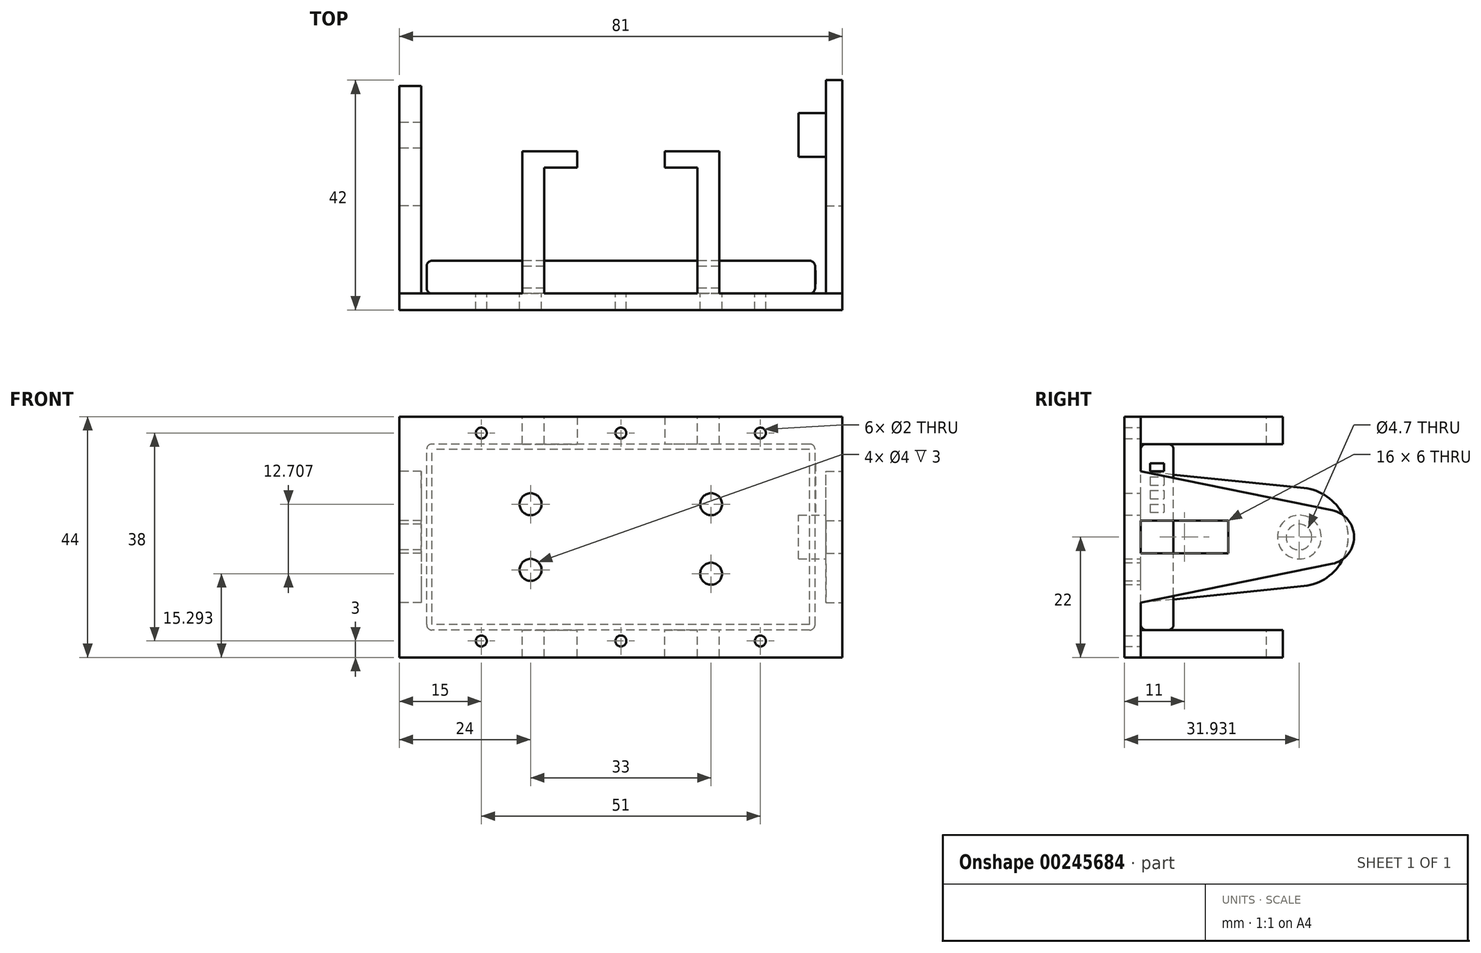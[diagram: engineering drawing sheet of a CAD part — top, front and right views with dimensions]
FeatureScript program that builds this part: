
annotation { "Feature Type Name" : "Feature", "Feature Type Description" : "" }
export const myFeature = defineFeature(function(context is Context, id is Id, definition is map)
    precondition{}
    {
        {
            var Q0;
            Q0=qCreatedBy(makeId("Front.planeOp"),FACE);
            var sketch = newSketch(context, id + "F0", { "sketchPlane" : qUnion([Q0])});
            skLineSegment(sketch, "E0.bottom", {"start": v(35.5, -17) * mm, "end": v(-35.5, -17) * mm});
            skLineSegment(sketch, "E0.top", {"start": v(35.5, 17) * mm, "end": v(-35.5, 17) * mm});
            skLineSegment(sketch, "E0.left", {"start": v(35.5, -17) * mm, "end": v(35.5, 17) * mm});
            skLineSegment(sketch, "E0.right", {"start": v(-35.5, -17) * mm, "end": v(-35.5, 17) * mm});
            skPoint(sketch, "E0.middle", {"position": v(0, 0) * mm});
            skSolve(sketch);
        }
        {
            var Q0;
            Q0=qSketchRegion(id+"F0",true);
            extrude(context, id + "F1", {"entities" : qUnion([Q0]), "endBound" : BoundingType.SYMMETRIC, "depth" : 6 * mm});
        }
        {
            var Q0;
            Q0=makeQuery(id+"F1.opExtrude","CAP_EDGE",EDGE,{"disambiguationData":[OSD([sQuery(id+"F0.wireOp",EDGE,"E0.top")])],"isStart":false});
            var Q1;
            Q1=makeQuery(id+"F1.opExtrude","CAP_EDGE",EDGE,{"disambiguationData":[OSD([sQuery(id+"F0.wireOp",EDGE,"E0.top")])],"isStart":true});
            var Q2;
            Q2=makeQuery(id+"F1.opExtrude","CAP_EDGE",EDGE,{"disambiguationData":[OSD([sQuery(id+"F0.wireOp",EDGE,"E0.left")])],"isStart":false});
            var Q3;
            Q3=makeQuery(id+"F1.opExtrude","CAP_EDGE",EDGE,{"disambiguationData":[OSD([sQuery(id+"F0.wireOp",EDGE,"E0.left")])],"isStart":true});
            var Q4;
            Q4=makeQuery(id+"F1.opExtrude","CAP_EDGE",EDGE,{"disambiguationData":[OSD([sQuery(id+"F0.wireOp",EDGE,"E0.bottom")])],"isStart":false});
            var Q5;
            Q5=makeQuery(id+"F1.opExtrude","SWEPT_EDGE",EDGE,{"disambiguationData":[OSD([sQuery(id+"F0.wireOp",EDGE,"E0.bottom"),sQuery(id+"F0.wireOp",EDGE,"E0.left")])]});
            var Q6;
            Q6=makeQuery(id+"F1.opExtrude","SWEPT_EDGE",EDGE,{"disambiguationData":[OSD([sQuery(id+"F0.wireOp",EDGE,"E0.top"),sQuery(id+"F0.wireOp",EDGE,"E0.right")])]});
            var Q7;
            Q7=makeQuery(id+"F1.opExtrude","CAP_EDGE",EDGE,{"disambiguationData":[OSD([sQuery(id+"F0.wireOp",EDGE,"E0.right")])],"isStart":false});
            var Q8;
            Q8=makeQuery(id+"F1.opExtrude","CAP_EDGE",EDGE,{"disambiguationData":[OSD([sQuery(id+"F0.wireOp",EDGE,"E0.right")])],"isStart":true});
            var Q9;
            Q9=makeQuery(id+"F1.opExtrude","CAP_EDGE",EDGE,{"disambiguationData":[OSD([sQuery(id+"F0.wireOp",EDGE,"E0.bottom")])],"isStart":true});
            var Q10;
            Q10=makeQuery(id+"F1.opExtrude","SWEPT_EDGE",EDGE,{"disambiguationData":[OSD([sQuery(id+"F0.wireOp",EDGE,"E0.bottom"),sQuery(id+"F0.wireOp",EDGE,"E0.right")])]});
            var Q11;
            Q11=makeQuery(id+"F1.opExtrude","SWEPT_EDGE",EDGE,{"disambiguationData":[OSD([sQuery(id+"F0.wireOp",EDGE,"E0.top"),sQuery(id+"F0.wireOp",EDGE,"E0.left")])]});
            fillet(context, id + "F2", {"entities" : qUnion([Q0, Q1, Q2, Q3, Q4, Q5, Q6, Q7, Q8, Q9, Q10, Q11]), "radius" : 1 * mm, "tangentPropagation" : true, "allowEdgeOverflow" : false});
        }
        {
            var Q0;
            Q0=makeQuery(id+"F1.opExtrude","SWEPT_FACE",FACE,{"disambiguationData":[OSD([sQuery(id+"F0.wireOp",EDGE,"E0.left")])]});
            var sketch = newSketch(context, id + "F3", { "sketchPlane" : qUnion([Q0])});
            skLineSegment(sketch, "E1.bottom", {"start": v(-1.25, 13.5) * mm, "end": v(1.25, 13.5) * mm});
            skLineSegment(sketch, "E1.top", {"start": v(-1.25, 12) * mm, "end": v(1.25, 12) * mm});
            skLineSegment(sketch, "E1.left", {"start": v(-1.25, 13.5) * mm, "end": v(-1.25, 12) * mm});
            skLineSegment(sketch, "E1.right", {"start": v(1.25, 13.5) * mm, "end": v(1.25, 12) * mm});
            skLineSegment(sketch, "E2.bottom", {"start": v(-1.25, 11) * mm, "end": v(1.25, 11) * mm});
            skLineSegment(sketch, "E2.top", {"start": v(-1.25, 9.5) * mm, "end": v(1.25, 9.5) * mm});
            skLineSegment(sketch, "E2.left", {"start": v(-1.25, 11) * mm, "end": v(-1.25, 9.5) * mm});
            skLineSegment(sketch, "E2.right", {"start": v(1.25, 11) * mm, "end": v(1.25, 9.5) * mm});
            skLineSegment(sketch, "E3.bottom", {"start": v(-1.25, 8.5) * mm, "end": v(1.25, 8.5) * mm});
            skLineSegment(sketch, "E3.top", {"start": v(-1.25, 7) * mm, "end": v(1.25, 7) * mm});
            skLineSegment(sketch, "E3.left", {"start": v(-1.25, 8.5) * mm, "end": v(-1.25, 7) * mm});
            skLineSegment(sketch, "E3.right", {"start": v(1.25, 8.5) * mm, "end": v(1.25, 7) * mm});
            skLineSegment(sketch, "E4.bottom", {"start": v(-1.25, 6) * mm, "end": v(1.25, 6) * mm});
            skLineSegment(sketch, "E4.top", {"start": v(-1.25, 4.5) * mm, "end": v(1.25, 4.5) * mm});
            skLineSegment(sketch, "E4.left", {"start": v(-1.25, 6) * mm, "end": v(-1.25, 4.5) * mm});
            skLineSegment(sketch, "E4.right", {"start": v(1.25, 6) * mm, "end": v(1.25, 4.5) * mm});
            skSolve(sketch);
        }
        {
            var Q0;
            Q0=qSketchRegion(id+"F3",true);
            extrude(context, id + "F4", {"entities" : qUnion([Q0]), "operationType" : NewBodyOperationType.ADD, "depth" : 0.1 * mm});
        }
        {
            var Q0;
            Q0=makeQuery(id+"F1.opExtrude","CAP_FACE",FACE,{"disambiguationData":[OSD([sQuery(id+"F0.wireOp",EDGE,"E0.bottom"),sQuery(id+"F0.wireOp",EDGE,"E0.top"),sQuery(id+"F0.wireOp",EDGE,"E0.left"),sQuery(id+"F0.wireOp",EDGE,"E0.right")])],"isStart":false});
            var sketch = newSketch(context, id + "F5", { "sketchPlane" : qUnion([Q0])});
            skLineSegment(sketch, "E5.0", {"start": v(40.5, 22) * mm, "end": v(-40.5, 22) * mm});
            skLineSegment(sketch, "E5.1", {"start": v(40.5, -22) * mm, "end": v(40.5, 22) * mm});
            skLineSegment(sketch, "E5.2", {"start": v(-40.5, -22) * mm, "end": v(40.5, -22) * mm});
            skLineSegment(sketch, "E5.3", {"start": v(-40.5, 22) * mm, "end": v(-40.5, -22) * mm});
            skCircle(sketch, "E6", {"center": v(16.5, 6) * mm, "radius": 2 * mm});
            skCircle(sketch, "E7", {"center": v(16.5, -6.7) * mm, "radius": 2 * mm});
            skCircle(sketch, "E8", {"center": v(-16.5, 6) * mm, "radius": 2 * mm});
            skCircle(sketch, "E9", {"center": v(-16.5, -6) * mm, "radius": 2 * mm});
            skSolve(sketch);
        }
        {
            var Q0;
            Q0=qSketchRegion(id+"F5",true);
            extrude(context, id + "F6", {"entities" : qUnion([Q0]), "depth" : 3 * mm});
        }
        {
            var Q0;
            Q0=makeQuery(id+"F6.opExtrude","SWEPT_FACE",FACE,{"disambiguationData":[OSD([sQuery(id+"F5.wireOp",EDGE,"E5.3")])]});
            var sketch = newSketch(context, id + "F7", { "sketchPlane" : qUnion([Q0])});
            skCircle(sketch, "E10", {"center": v(-25.93, 0) * mm, "radius": 9 * mm});
            skLineSegment(sketch, "E11", {"start": v(-26.84, -8.95) * mm, "end": v(3, -12) * mm});
            skLineSegment(sketch, "E12", {"start": v(-26.84, 8.95) * mm, "end": v(3, 12) * mm});
            skLineSegment(sketch, "E13", {"start": v(3, 12) * mm, "end": v(3, 3) * mm});
            skLineSegment(sketch, "E14.bottom", {"start": v(-13, -3) * mm, "end": v(3, -3) * mm});
            skLineSegment(sketch, "E14.top", {"start": v(-13, 3) * mm, "end": v(3, 3) * mm});
            skLineSegment(sketch, "E14.left", {"start": v(-13, -3) * mm, "end": v(-13, 3) * mm});
            skLineSegment(sketch, "E15.trimOffspring", {"start": v(3, -3) * mm, "end": v(3, -12) * mm});
            skCircle(sketch, "E16", {"center": v(-25.93, 0) * mm, "radius": 2.35 * mm});
            skSolve(sketch);
        }
        {
            var Q0;
            Q0=qSketchRegion(id+"F7",true);
            extrude(context, id + "F8", {"entities" : qUnion([Q0]), "operationType" : NewBodyOperationType.ADD, "oppositeDirection" : true, "depth" : 4 * mm});
        }
        {
            var Q0;
            Q0=makeQuery(id+"F6.opExtrude","SWEPT_FACE",FACE,{"disambiguationData":[OSD([sQuery(id+"F5.wireOp",EDGE,"E5.1")])]});
            var sketch = newSketch(context, id + "F9", { "sketchPlane" : qUnion([Q0])});
            skCircle(sketch, "E17", {"center": v(31, 0) * mm, "radius": 5 * mm});
            skLineSegment(sketch, "E18", {"start": v(32, 4.9) * mm, "end": v(-3, 12) * mm});
            skLineSegment(sketch, "E19", {"start": v(32, -4.9) * mm, "end": v(-3, -12) * mm});
            skLineSegment(sketch, "E20", {"start": v(-3, -12) * mm, "end": v(-3, -3) * mm});
            skLineSegment(sketch, "E21.bottom", {"start": v(-3, 3) * mm, "end": v(13, 3) * mm});
            skLineSegment(sketch, "E21.top", {"start": v(-3, -3) * mm, "end": v(13, -3) * mm});
            skLineSegment(sketch, "E21.right", {"start": v(13, 3) * mm, "end": v(13, -3) * mm});
            skLineSegment(sketch, "E22.trimOffspring", {"start": v(-3, 3) * mm, "end": v(-3, 12) * mm});
            skSolve(sketch);
        }
        {
            var Q0;
            Q0=qSketchRegion(id+"F9",true);
            extrude(context, id + "F10", {"entities" : qUnion([Q0]), "operationType" : NewBodyOperationType.ADD, "oppositeDirection" : true, "depth" : 3 * mm});
        }
        {
            var Q0;
            Q0=makeQuery(id+"F10.boolean.opBoolean","MERGE",FACE,{"derivedFrom":[makeQuery(id+"F6.opExtrude","SWEPT_FACE",FACE,{"disambiguationData":[OSD([sQuery(id+"F5.wireOp",EDGE,"E5.1")])]}),makeQuery(id+"F10.opExtrude","CAP_FACE",FACE,{"disambiguationData":[OSD([sQuery(id+"F9.wireOp",EDGE,"E17"),sQuery(id+"F9.wireOp",EDGE,"E18"),sQuery(id+"F9.wireOp",EDGE,"E19"),sQuery(id+"F9.wireOp",EDGE,"E20"),sQuery(id+"F9.wireOp",EDGE,"E21.bottom"),sQuery(id+"F9.wireOp",EDGE,"E21.top"),sQuery(id+"F9.wireOp",EDGE,"E21.right"),sQuery(id+"F9.wireOp",EDGE,"E22.trimOffspring")])],"isStart":true})]});
            var sketch = newSketch(context, id + "F11", { "sketchPlane" : qUnion([Q0])});
            skCircle(sketch, "E23", {"center": v(26, 0) * mm, "radius": 4 * mm});
            skSolve(sketch);
        }
        {
            var Q0;
            Q0=qSketchRegion(id+"F11",true);
            extrude(context, id + "F12", {"entities" : qUnion([Q0]), "operationType" : NewBodyOperationType.ADD, "oppositeDirection" : true, "depth" : 8 * mm});
        }
        {
            var Q0;
            Q0=makeQuery(id+"F6.opExtrude","CAP_FACE",FACE,{"disambiguationData":[OSD([sQuery(id+"F5.wireOp",EDGE,"E5.0"),sQuery(id+"F5.wireOp",EDGE,"E5.1"),sQuery(id+"F5.wireOp",EDGE,"E5.2"),sQuery(id+"F5.wireOp",EDGE,"E5.3")])],"isStart":true});
            var sketch = newSketch(context, id + "F13", { "sketchPlane" : qUnion([Q0])});
            skLineSegment(sketch, "E24.bottom", {"start": v(18, 17) * mm, "end": v(14, 17) * mm});
            skLineSegment(sketch, "E24.top", {"start": v(18, 22) * mm, "end": v(14, 22) * mm});
            skLineSegment(sketch, "E24.left", {"start": v(18, 17) * mm, "end": v(18, 22) * mm});
            skLineSegment(sketch, "E24.right", {"start": v(14, 17) * mm, "end": v(14, 22) * mm});
            skLineSegment(sketch, "E25.bottom", {"start": v(-14, 17) * mm, "end": v(-18, 17) * mm});
            skLineSegment(sketch, "E25.top", {"start": v(-14, 22) * mm, "end": v(-18, 22) * mm});
            skLineSegment(sketch, "E25.left", {"start": v(-14, 17) * mm, "end": v(-14, 22) * mm});
            skLineSegment(sketch, "E25.right", {"start": v(-18, 17) * mm, "end": v(-18, 22) * mm});
            skLineSegment(sketch, "E26.bottom", {"start": v(18, -22) * mm, "end": v(14, -22) * mm});
            skLineSegment(sketch, "E26.top", {"start": v(18, -17) * mm, "end": v(14, -17) * mm});
            skLineSegment(sketch, "E26.left", {"start": v(18, -22) * mm, "end": v(18, -17) * mm});
            skLineSegment(sketch, "E26.right", {"start": v(14, -22) * mm, "end": v(14, -17) * mm});
            skLineSegment(sketch, "E27.bottom", {"start": v(-14, -22) * mm, "end": v(-18, -22) * mm});
            skLineSegment(sketch, "E27.top", {"start": v(-14, -17) * mm, "end": v(-18, -17) * mm});
            skLineSegment(sketch, "E27.left", {"start": v(-14, -22) * mm, "end": v(-14, -17) * mm});
            skLineSegment(sketch, "E27.right", {"start": v(-18, -22) * mm, "end": v(-18, -17) * mm});
            skSolve(sketch);
        }
        {
            var Q0;
            Q0=qSketchRegion(id+"F13",true);
            extrude(context, id + "F14", {"entities" : qUnion([Q0]), "operationType" : NewBodyOperationType.ADD, "depth" : 23 * mm});
        }
        {
            var Q0;
            Q0=makeQuery(id+"F14.opExtrude","SWEPT_FACE",FACE,{"disambiguationData":[OSD([sQuery(id+"F13.wireOp",EDGE,"E24.bottom")])]});
            var sketch = newSketch(context, id + "F15", { "sketchPlane" : qUnion([Q0])});
            skLineSegment(sketch, "E28.bottom", {"start": v(18, -20) * mm, "end": v(8, -20) * mm});
            skLineSegment(sketch, "E28.top", {"start": v(18, -23) * mm, "end": v(8, -23) * mm});
            skLineSegment(sketch, "E28.left", {"start": v(18, -20) * mm, "end": v(18, -23) * mm});
            skLineSegment(sketch, "E28.right", {"start": v(8, -20) * mm, "end": v(8, -23) * mm});
            skLineSegment(sketch, "E29.bottom", {"start": v(-18, -20) * mm, "end": v(-8, -20) * mm});
            skLineSegment(sketch, "E29.top", {"start": v(-18, -23) * mm, "end": v(-8, -23) * mm});
            skLineSegment(sketch, "E29.left", {"start": v(-18, -20) * mm, "end": v(-18, -23) * mm});
            skLineSegment(sketch, "E29.right", {"start": v(-8, -20) * mm, "end": v(-8, -23) * mm});
            skSolve(sketch);
        }
        {
            var Q0;
            Q0=qSketchRegion(id+"F15",true);
            extrude(context, id + "F16", {"entities" : qUnion([Q0]), "operationType" : NewBodyOperationType.ADD, "oppositeDirection" : true, "depth" : 5 * mm});
        }
        {
            var Q0;
            Q0=makeQuery(id+"F6.opExtrude","CAP_FACE",FACE,{"disambiguationData":[OSD([sQuery(id+"F5.wireOp",EDGE,"E5.0"),sQuery(id+"F5.wireOp",EDGE,"E5.1"),sQuery(id+"F5.wireOp",EDGE,"E5.2"),sQuery(id+"F5.wireOp",EDGE,"E5.3")])],"isStart":true});
            var sketch = newSketch(context, id + "F17", { "sketchPlane" : qUnion([Q0])});
            skCircle(sketch, "E30", {"center": v(25.5, 19) * mm, "radius": 1 * mm});
            skCircle(sketch, "E31", {"center": v(25.5, -19) * mm, "radius": 1 * mm});
            skCircle(sketch, "E32", {"center": v(-25.5, 19) * mm, "radius": 1 * mm});
            skCircle(sketch, "E33", {"center": v(-25.5, -19) * mm, "radius": 1 * mm});
            skCircle(sketch, "E34", {"center": v(0, -19) * mm, "radius": 1 * mm});
            skCircle(sketch, "E35", {"center": v(0, 19) * mm, "radius": 1 * mm});
            skSolve(sketch);
        }
        {
            var Q0;
            Q0=qSketchRegion(id+"F17",true);
            extrude(context, id + "F18", {"entities" : qUnion([Q0]), "operationType" : NewBodyOperationType.REMOVE, "oppositeDirection" : true, "depth" : 25 * mm});
        }
        {
            var Q0;
            Q0=makeQuery(id+"F14.opExtrude","SWEPT_FACE",FACE,{"disambiguationData":[OSD([sQuery(id+"F13.wireOp",EDGE,"E26.top")])]});
            var sketch = newSketch(context, id + "F19", { "sketchPlane" : qUnion([Q0])});
            skLineSegment(sketch, "E36.bottom", {"start": v(-18, 20) * mm, "end": v(-8, 20) * mm});
            skLineSegment(sketch, "E36.top", {"start": v(-18, 23) * mm, "end": v(-8, 23) * mm});
            skLineSegment(sketch, "E36.left", {"start": v(-18, 20) * mm, "end": v(-18, 23) * mm});
            skLineSegment(sketch, "E36.right", {"start": v(-8, 20) * mm, "end": v(-8, 23) * mm});
            skLineSegment(sketch, "E37.top", {"start": v(18, 23) * mm, "end": v(8, 23) * mm});
            skLineSegment(sketch, "E37.left", {"start": v(18, 20) * mm, "end": v(18, 23) * mm});
            skLineSegment(sketch, "E37.right", {"start": v(8, 20) * mm, "end": v(8, 23) * mm});
            skLineSegment(sketch, "E38", {"start": v(8, 20) * mm, "end": v(18, 20) * mm});
            skSolve(sketch);
        }
        {
            var Q0;
            Q0 = qSketchRegion(id + "F19", true);
            extrude(context, id + "F20", {"entities" : qUnion([Q0]), "operationType" : NewBodyOperationType.ADD, "oppositeDirection" : true, "depth" : 5 * mm});
        }
    });
